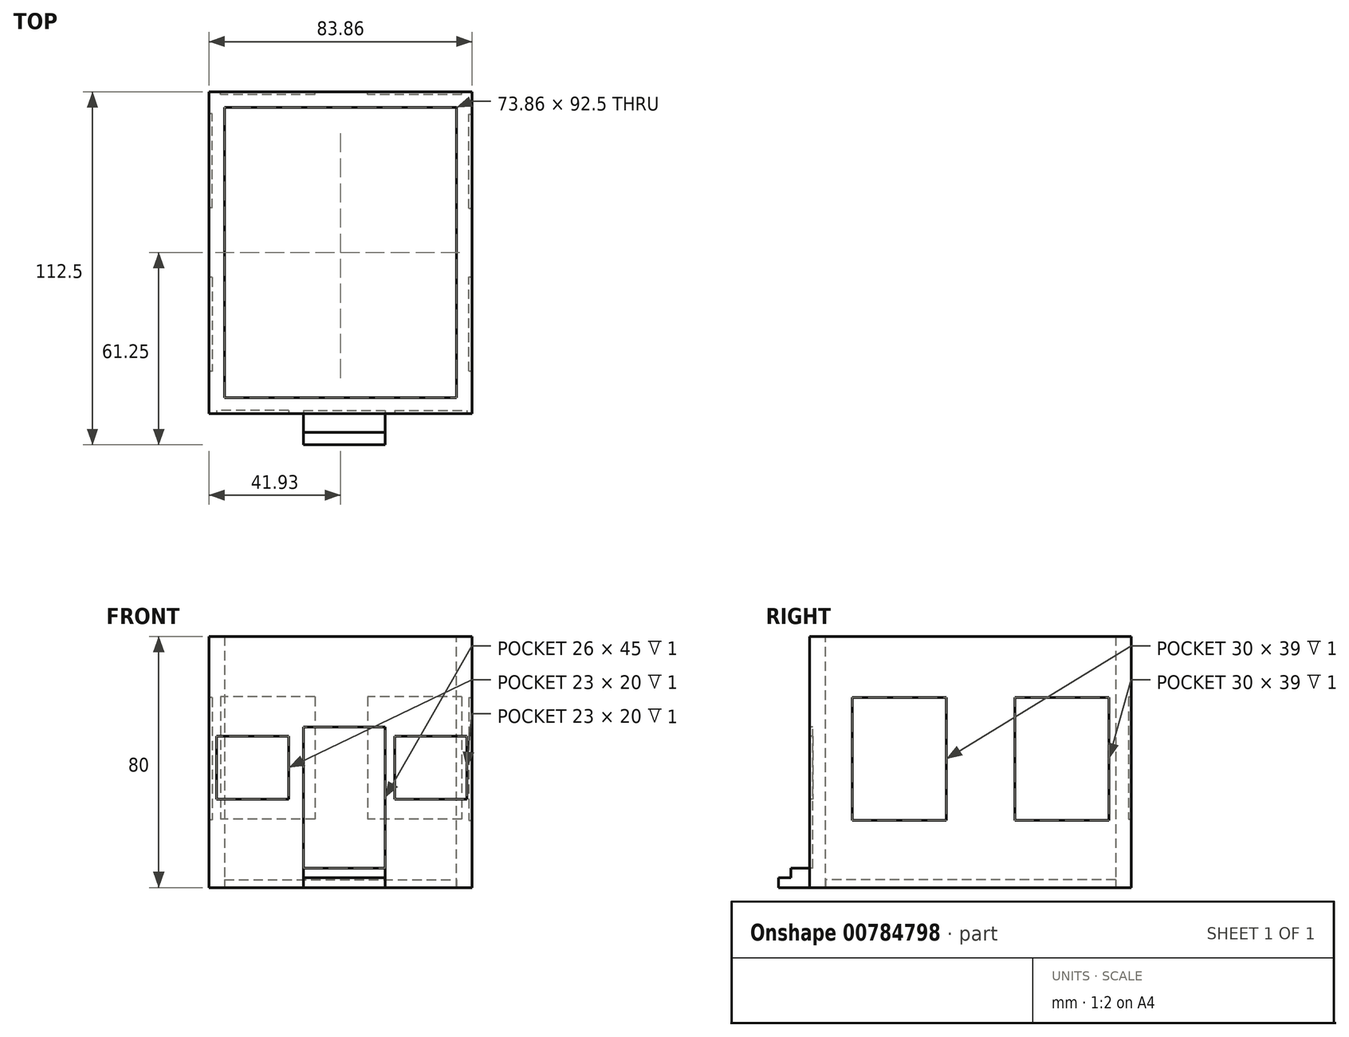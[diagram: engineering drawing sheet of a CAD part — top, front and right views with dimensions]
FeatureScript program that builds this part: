
annotation { "Feature Type Name" : "Feature", "Feature Type Description" : "" }
export const myFeature = defineFeature(function(context is Context, id is Id, definition is map)
    precondition{}
    {
        {
            var Q0;
            Q0=qCreatedBy(makeId("Front.planeOp"),FACE);
            var sketch = newSketch(context, id + "F0", { "sketchPlane" : qUnion([Q0])});
            skLineSegment(sketch, "E0.bottom", {"start": v(-40.68, 40) * mm, "end": v(40.68, 40) * mm});
            skLineSegment(sketch, "E0.top", {"start": v(-40.68, -40) * mm, "end": v(40.68, -40) * mm});
            skLineSegment(sketch, "E0.left", {"start": v(-40.68, 40) * mm, "end": v(-40.68, -40) * mm});
            skLineSegment(sketch, "E0.right", {"start": v(40.68, 40) * mm, "end": v(40.68, -40) * mm});
            skPoint(sketch, "E0.middle", {"position": v(0, 0) * mm});
            skSolve(sketch);
        }
        {
            var Q0;
            Q0 = qSketchRegion(id + "F0", true);
            extrude(context, id + "F1", {"entities" : qUnion([Q0]), "depth" : 2.5 * mm, "offsetDistance" : 25 * mm, "hasSecondDirection" : true, "secondDirectionOppositeDirection" : true, "secondDirectionDepth" : 2.5 * mm});
        }
        {
            var Q0;
            Q0=makeQuery(id+"F1.opExtrude","SWEPT_FACE",FACE,{"disambiguationData":[OSD([sQuery(id+"F0.wireOp",EDGE,"E0.left")])]});
            var sketch = newSketch(context, id + "F2", { "sketchPlane" : qUnion([Q0])});
            skLineSegment(sketch, "E1.bottom", {"start": v(2.5, 40) * mm, "end": v(-97.5, 40) * mm});
            skLineSegment(sketch, "E1.top", {"start": v(2.5, -40) * mm, "end": v(-97.5, -40) * mm});
            skLineSegment(sketch, "E1.left", {"start": v(2.5, 40) * mm, "end": v(2.5, -40) * mm});
            skLineSegment(sketch, "E1.right", {"start": v(-97.5, 40) * mm, "end": v(-97.5, -40) * mm});
            skSolve(sketch);
        }
        {
            var Q0;
            Q0 = qSketchRegion(id + "F2", true);
            extrude(context, id + "F3", {"entities" : qUnion([Q0]), "operationType" : NewBodyOperationType.ADD, "depth" : 2.5 * mm, "offsetDistance" : 25 * mm, "hasSecondDirection" : true, "secondDirectionOppositeDirection" : true, "secondDirectionDepth" : 2.5 * mm});
        }
        {
            var Q0;
            Q0=makeQuery(id+"F3.opExtrude","SWEPT_FACE",FACE,{"disambiguationData":[OSD([sQuery(id+"F2.wireOp",EDGE,"E1.right")])]});
            var sketch = newSketch(context, id + "F4", { "sketchPlane" : qUnion([Q0])});
            skLineSegment(sketch, "E2.bottom", {"start": v(43.18, 40) * mm, "end": v(-38.18, 40) * mm});
            skLineSegment(sketch, "E2.top", {"start": v(43.18, -40) * mm, "end": v(-38.18, -40) * mm});
            skLineSegment(sketch, "E2.left", {"start": v(43.18, 40) * mm, "end": v(43.18, -40) * mm});
            skLineSegment(sketch, "E2.right", {"start": v(-38.18, 40) * mm, "end": v(-38.18, -40) * mm});
            skSolve(sketch);
        }
        {
            var Q0;
            Q0 = qSketchRegion(id + "F4", true);
            extrude(context, id + "F5", {"entities" : qUnion([Q0]), "operationType" : NewBodyOperationType.ADD, "depth" : 2.5 * mm, "offsetDistance" : 25 * mm, "hasSecondDirection" : true, "secondDirectionOppositeDirection" : true, "secondDirectionDepth" : 2.5 * mm});
        }
        {
            var Q0;
            Q0=makeQuery(id+"F5.opExtrude","SWEPT_FACE",FACE,{"disambiguationData":[OSD([sQuery(id+"F4.wireOp",EDGE,"E2.right")])]});
            var sketch = newSketch(context, id + "F6", { "sketchPlane" : qUnion([Q0])});
            skLineSegment(sketch, "E3.bottom", {"start": v(100, 40) * mm, "end": v(0, 40) * mm});
            skLineSegment(sketch, "E3.top", {"start": v(100, -40) * mm, "end": v(0, -40) * mm});
            skLineSegment(sketch, "E3.left", {"start": v(100, 40) * mm, "end": v(100, -40) * mm});
            skLineSegment(sketch, "E3.right", {"start": v(0, 40) * mm, "end": v(0, -40) * mm});
            skSolve(sketch);
        }
        {
            var Q0;
            Q0 = qSketchRegion(id + "F6", true);
            extrude(context, id + "F7", {"entities" : qUnion([Q0]), "operationType" : NewBodyOperationType.ADD, "depth" : 2.5 * mm, "offsetDistance" : 25 * mm, "hasSecondDirection" : true, "secondDirectionOppositeDirection" : true, "secondDirectionDepth" : 2.5 * mm});
        }
        {
            var Q0;
            Q0=makeQuery(id+"F7.boolean.opBoolean","MERGE",FACE,{"derivedFrom":[makeQuery(id+"F5.boolean.opBoolean","MERGE",FACE,{"derivedFrom":[makeQuery(id+"F3.boolean.opBoolean","MERGE",FACE,{"derivedFrom":[makeQuery(id+"F1.opExtrude","SWEPT_FACE",FACE,{"disambiguationData":[OSD([sQuery(id+"F0.wireOp",EDGE,"E0.top")])]}),makeQuery(id+"F3.opExtrude","SWEPT_FACE",FACE,{"disambiguationData":[OSD([sQuery(id+"F2.wireOp",EDGE,"E1.top")])]})]}),makeQuery(id+"F5.opExtrude","SWEPT_FACE",FACE,{"disambiguationData":[OSD([sQuery(id+"F4.wireOp",EDGE,"E2.top")])]})]}),makeQuery(id+"F7.opExtrude","SWEPT_FACE",FACE,{"disambiguationData":[OSD([sQuery(id+"F6.wireOp",EDGE,"E3.top")])]})]});
            var sketch = newSketch(context, id + "F8", { "sketchPlane" : qUnion([Q0])});
            skLineSegment(sketch, "E4.bottom", {"start": v(35.68, -2.5) * mm, "end": v(-38.18, -2.5) * mm});
            skLineSegment(sketch, "E4.top", {"start": v(35.68, -95) * mm, "end": v(-38.18, -95) * mm});
            skLineSegment(sketch, "E4.left", {"start": v(35.68, -2.5) * mm, "end": v(35.68, -95) * mm});
            skLineSegment(sketch, "E4.right", {"start": v(-38.18, -2.5) * mm, "end": v(-38.18, -95) * mm});
            skSolve(sketch);
        }
        {
            var Q0;
            Q0 = qSketchRegion(id + "F8", true);
            extrude(context, id + "F9", {"entities" : qUnion([Q0]), "depth" : 0 * mm, "offsetDistance" : 25 * mm, "hasSecondDirection" : true, "secondDirectionOppositeDirection" : true, "secondDirectionDepth" : 2.5 * mm});
        }
        {
            var Q0;
            Q0=makeQuery(id+"F3.boolean.opBoolean","MERGE",FACE,{"derivedFrom":[makeQuery(id+"F1.opExtrude","CAP_FACE",FACE,{"disambiguationData":[OSD([sQuery(id+"F0.wireOp",EDGE,"E0.bottom"),sQuery(id+"F0.wireOp",EDGE,"E0.top"),sQuery(id+"F0.wireOp",EDGE,"E0.left"),sQuery(id+"F0.wireOp",EDGE,"E0.right")])],"isStart":false}),makeQuery(id+"F3.opExtrude","SWEPT_FACE",FACE,{"disambiguationData":[OSD([sQuery(id+"F2.wireOp",EDGE,"E1.left")])]})]});
            var sketch = newSketch(context, id + "F10", { "sketchPlane" : qUnion([Q0])});
            skLineSegment(sketch, "E5.bottom", {"start": v(-13, -33.85) * mm, "end": v(13, -33.85) * mm});
            skLineSegment(sketch, "E5.top", {"start": v(-13, 11.15) * mm, "end": v(13, 11.15) * mm});
            skLineSegment(sketch, "E5.left", {"start": v(-13, -33.85) * mm, "end": v(-13, 11.15) * mm});
            skLineSegment(sketch, "E5.right", {"start": v(13, -33.85) * mm, "end": v(13, 11.15) * mm});
            skPoint(sketch, "E5.middle", {"position": v(0, -11.35) * mm});
            skSolve(sketch);
        }
        {
            var Q0;
            Q0 = qSketchRegion(id + "F10", true);
            extrude(context, id + "F11", {"entities" : qUnion([Q0]), "operationType" : NewBodyOperationType.REMOVE, "oppositeDirection" : true, "depth" : 1 * mm, "offsetDistance" : 25 * mm, "hasSecondDirection" : true, "secondDirectionOppositeDirection" : false, "secondDirectionDepth" : 0 * mm});
        }
        {
            var Q0;
            Q0=makeQuery(id+"F3.boolean.opBoolean","MERGE",FACE,{"derivedFrom":[makeQuery(id+"F1.opExtrude","CAP_FACE",FACE,{"disambiguationData":[OSD([sQuery(id+"F0.wireOp",EDGE,"E0.bottom"),sQuery(id+"F0.wireOp",EDGE,"E0.top"),sQuery(id+"F0.wireOp",EDGE,"E0.left"),sQuery(id+"F0.wireOp",EDGE,"E0.right")])],"isStart":false}),makeQuery(id+"F3.opExtrude","SWEPT_FACE",FACE,{"disambiguationData":[OSD([sQuery(id+"F2.wireOp",EDGE,"E1.left")])]})]});
            var sketch = newSketch(context, id + "F12", { "sketchPlane" : qUnion([Q0])});
            skLineSegment(sketch, "E6.bottom", {"start": v(-13, -33.85) * mm, "end": v(13, -33.85) * mm});
            skLineSegment(sketch, "E6.top", {"start": v(-13, -40) * mm, "end": v(13, -40) * mm});
            skLineSegment(sketch, "E6.left", {"start": v(-13, -33.85) * mm, "end": v(-13, -40) * mm});
            skLineSegment(sketch, "E6.right", {"start": v(13, -33.85) * mm, "end": v(13, -40) * mm});
            skSolve(sketch);
        }
        {
            var Q0;
            Q0 = qSketchRegion(id + "F12", true);
            extrude(context, id + "F13", {"entities" : qUnion([Q0]), "operationType" : NewBodyOperationType.ADD, "depth" : 6 * mm, "offsetDistance" : 25 * mm});
        }
        {
            var Q0;
            Q0=makeQuery(id+"F3.boolean.opBoolean","MERGE",FACE,{"derivedFrom":[makeQuery(id+"F1.opExtrude","CAP_FACE",FACE,{"disambiguationData":[OSD([sQuery(id+"F0.wireOp",EDGE,"E0.bottom"),sQuery(id+"F0.wireOp",EDGE,"E0.top"),sQuery(id+"F0.wireOp",EDGE,"E0.left"),sQuery(id+"F0.wireOp",EDGE,"E0.right")])],"isStart":false}),makeQuery(id+"F3.opExtrude","SWEPT_FACE",FACE,{"disambiguationData":[OSD([sQuery(id+"F2.wireOp",EDGE,"E1.left")])]})]});
            var sketch = newSketch(context, id + "F14", { "sketchPlane" : qUnion([Q0])});
            skLineSegment(sketch, "E7.bottom", {"start": v(-17.77, 8.2) * mm, "end": v(-40.77, 8.2) * mm});
            skLineSegment(sketch, "E7.top", {"start": v(-17.77, -11.8) * mm, "end": v(-40.77, -11.8) * mm});
            skLineSegment(sketch, "E7.left", {"start": v(-17.77, 8.2) * mm, "end": v(-17.77, -11.8) * mm});
            skLineSegment(sketch, "E7.right", {"start": v(-40.77, 8.2) * mm, "end": v(-40.77, -11.8) * mm});
            skSolve(sketch);
        }
        {
            var Q0;
            Q0 = qSketchRegion(id + "F14", true);
            extrude(context, id + "F15", {"entities" : qUnion([Q0]), "operationType" : NewBodyOperationType.REMOVE, "oppositeDirection" : true, "depth" : 1 * mm, "offsetDistance" : 25 * mm});
        }
        {
            var Q0;
            Q0=makeQuery(id+"F3.boolean.opBoolean","MERGE",FACE,{"derivedFrom":[makeQuery(id+"F1.opExtrude","CAP_FACE",FACE,{"disambiguationData":[OSD([sQuery(id+"F0.wireOp",EDGE,"E0.bottom"),sQuery(id+"F0.wireOp",EDGE,"E0.top"),sQuery(id+"F0.wireOp",EDGE,"E0.left"),sQuery(id+"F0.wireOp",EDGE,"E0.right")])],"isStart":false}),makeQuery(id+"F3.opExtrude","SWEPT_FACE",FACE,{"disambiguationData":[OSD([sQuery(id+"F2.wireOp",EDGE,"E1.left")])]})]});
            var sketch = newSketch(context, id + "F16", { "sketchPlane" : qUnion([Q0])});
            skLineSegment(sketch, "E8.bottom", {"start": v(16.06, 8.2) * mm, "end": v(39.06, 8.2) * mm});
            skLineSegment(sketch, "E8.top", {"start": v(16.06, -11.8) * mm, "end": v(39.06, -11.8) * mm});
            skLineSegment(sketch, "E8.left", {"start": v(16.06, 8.2) * mm, "end": v(16.06, -11.8) * mm});
            skLineSegment(sketch, "E8.right", {"start": v(39.06, 8.2) * mm, "end": v(39.06, -11.8) * mm});
            skSolve(sketch);
        }
        {
            var Q0;
            Q0 = qSketchRegion(id + "F16", true);
            extrude(context, id + "F17", {"entities" : qUnion([Q0]), "operationType" : NewBodyOperationType.REMOVE, "oppositeDirection" : true, "depth" : 1 * mm, "offsetDistance" : 25 * mm});
        }
        {
            var Q0;
            Q0=makeQuery(id+"F3.boolean.opBoolean","MERGE",FACE,{"derivedFrom":[makeQuery(id+"F1.opExtrude","CAP_FACE",FACE,{"disambiguationData":[OSD([sQuery(id+"F0.wireOp",EDGE,"E0.bottom"),sQuery(id+"F0.wireOp",EDGE,"E0.top"),sQuery(id+"F0.wireOp",EDGE,"E0.left"),sQuery(id+"F0.wireOp",EDGE,"E0.right")])],"isStart":false}),makeQuery(id+"F3.opExtrude","SWEPT_FACE",FACE,{"disambiguationData":[OSD([sQuery(id+"F2.wireOp",EDGE,"E1.left")])]})]});
            var sketch = newSketch(context, id + "F18", { "sketchPlane" : qUnion([Q0])});
            skLineSegment(sketch, "E9.bottom", {"start": v(-13, -36.93) * mm, "end": v(13, -36.93) * mm});
            skLineSegment(sketch, "E9.top", {"start": v(-13, -40) * mm, "end": v(13, -40) * mm});
            skLineSegment(sketch, "E9.left", {"start": v(-13, -36.93) * mm, "end": v(-13, -40) * mm});
            skLineSegment(sketch, "E9.right", {"start": v(13, -36.93) * mm, "end": v(13, -40) * mm});
            skSolve(sketch);
        }
        {
            var Q0;
            Q0 = qSketchRegion(id + "F18", true);
            extrude(context, id + "F19", {"entities" : qUnion([Q0]), "operationType" : NewBodyOperationType.ADD, "depth" : 10 * mm, "offsetDistance" : 25 * mm});
        }
        {
            var Q0;
            Q0=makeQuery(id+"F5.boolean.opBoolean","MERGE",FACE,{"derivedFrom":[makeQuery(id+"F3.opExtrude","CAP_FACE",FACE,{"disambiguationData":[OSD([sQuery(id+"F2.wireOp",EDGE,"E1.bottom"),sQuery(id+"F2.wireOp",EDGE,"E1.top"),sQuery(id+"F2.wireOp",EDGE,"E1.left"),sQuery(id+"F2.wireOp",EDGE,"E1.right")])],"isStart":false}),makeQuery(id+"F5.opExtrude","SWEPT_FACE",FACE,{"disambiguationData":[OSD([sQuery(id+"F4.wireOp",EDGE,"E2.left")])]})]});
            var sketch = newSketch(context, id + "F20", { "sketchPlane" : qUnion([Q0])});
            skLineSegment(sketch, "E10.bottom", {"start": v(-40.86, 20.51) * mm, "end": v(-10.86, 20.51) * mm});
            skLineSegment(sketch, "E10.top", {"start": v(-40.86, -18.49) * mm, "end": v(-10.86, -18.49) * mm});
            skLineSegment(sketch, "E10.left", {"start": v(-40.86, 20.51) * mm, "end": v(-40.86, -18.49) * mm});
            skLineSegment(sketch, "E10.right", {"start": v(-10.86, 20.51) * mm, "end": v(-10.86, -18.49) * mm});
            skSolve(sketch);
        }
        {
            var Q0;
            Q0 = qSketchRegion(id + "F20", true);
            extrude(context, id + "F21", {"entities" : qUnion([Q0]), "operationType" : NewBodyOperationType.REMOVE, "oppositeDirection" : true, "depth" : 1 * mm, "offsetDistance" : 25 * mm});
        }
        {
            var Q0;
            Q0=makeQuery(id+"F5.boolean.opBoolean","MERGE",FACE,{"derivedFrom":[makeQuery(id+"F3.opExtrude","CAP_FACE",FACE,{"disambiguationData":[OSD([sQuery(id+"F2.wireOp",EDGE,"E1.bottom"),sQuery(id+"F2.wireOp",EDGE,"E1.top"),sQuery(id+"F2.wireOp",EDGE,"E1.left"),sQuery(id+"F2.wireOp",EDGE,"E1.right")])],"isStart":false}),makeQuery(id+"F5.opExtrude","SWEPT_FACE",FACE,{"disambiguationData":[OSD([sQuery(id+"F4.wireOp",EDGE,"E2.left")])]})]});
            var sketch = newSketch(context, id + "F22", { "sketchPlane" : qUnion([Q0])});
            skLineSegment(sketch, "E11.bottom", {"start": v(-62.94, 20.51) * mm, "end": v(-92.94, 20.51) * mm});
            skLineSegment(sketch, "E11.top", {"start": v(-62.94, -18.49) * mm, "end": v(-92.94, -18.49) * mm});
            skLineSegment(sketch, "E11.left", {"start": v(-62.94, 20.51) * mm, "end": v(-62.94, -18.49) * mm});
            skLineSegment(sketch, "E11.right", {"start": v(-92.94, 20.51) * mm, "end": v(-92.94, -18.49) * mm});
            skSolve(sketch);
        }
        {
            var Q0;
            Q0 = qSketchRegion(id + "F22", true);
            extrude(context, id + "F23", {"entities" : qUnion([Q0]), "operationType" : NewBodyOperationType.REMOVE, "depth" : 0 * mm, "offsetDistance" : 25 * mm, "hasSecondDirection" : true, "secondDirectionOppositeDirection" : true, "secondDirectionDepth" : 1 * mm});
        }
        {
            var Q0;
            Q0=makeQuery(id+"F7.boolean.opBoolean","MERGE",FACE,{"derivedFrom":[makeQuery(id+"F1.opExtrude","SWEPT_FACE",FACE,{"disambiguationData":[OSD([sQuery(id+"F0.wireOp",EDGE,"E0.right")])]}),makeQuery(id+"F7.opExtrude","CAP_FACE",FACE,{"disambiguationData":[OSD([sQuery(id+"F6.wireOp",EDGE,"E3.bottom"),sQuery(id+"F6.wireOp",EDGE,"E3.top"),sQuery(id+"F6.wireOp",EDGE,"E3.left"),sQuery(id+"F6.wireOp",EDGE,"E3.right")])],"isStart":false})]});
            var sketch = newSketch(context, id + "F24", { "sketchPlane" : qUnion([Q0])});
            skLineSegment(sketch, "E12.bottom", {"start": v(11, 20.47) * mm, "end": v(41, 20.47) * mm});
            skLineSegment(sketch, "E12.top", {"start": v(11, -18.53) * mm, "end": v(41, -18.53) * mm});
            skLineSegment(sketch, "E12.left", {"start": v(11, 20.47) * mm, "end": v(11, -18.53) * mm});
            skLineSegment(sketch, "E12.right", {"start": v(41, 20.47) * mm, "end": v(41, -18.53) * mm});
            skSolve(sketch);
        }
        {
            var Q0;
            Q0 = qSketchRegion(id + "F24", true);
            extrude(context, id + "F25", {"entities" : qUnion([Q0]), "operationType" : NewBodyOperationType.REMOVE, "oppositeDirection" : true, "depth" : 1 * mm, "offsetDistance" : 25 * mm});
        }
        {
            var Q0;
            Q0=makeQuery(id+"F7.boolean.opBoolean","MERGE",FACE,{"derivedFrom":[makeQuery(id+"F1.opExtrude","SWEPT_FACE",FACE,{"disambiguationData":[OSD([sQuery(id+"F0.wireOp",EDGE,"E0.right")])]}),makeQuery(id+"F7.opExtrude","CAP_FACE",FACE,{"disambiguationData":[OSD([sQuery(id+"F6.wireOp",EDGE,"E3.bottom"),sQuery(id+"F6.wireOp",EDGE,"E3.top"),sQuery(id+"F6.wireOp",EDGE,"E3.left"),sQuery(id+"F6.wireOp",EDGE,"E3.right")])],"isStart":false})]});
            var sketch = newSketch(context, id + "F26", { "sketchPlane" : qUnion([Q0])});
            skLineSegment(sketch, "E13.bottom", {"start": v(62.81, 20.47) * mm, "end": v(92.81, 20.47) * mm});
            skLineSegment(sketch, "E13.top", {"start": v(62.81, -18.53) * mm, "end": v(92.81, -18.53) * mm});
            skLineSegment(sketch, "E13.left", {"start": v(62.81, 20.47) * mm, "end": v(62.81, -18.53) * mm});
            skLineSegment(sketch, "E13.right", {"start": v(92.81, 20.47) * mm, "end": v(92.81, -18.53) * mm});
            skSolve(sketch);
        }
        {
            var Q0;
            Q0 = qSketchRegion(id + "F26", true);
            extrude(context, id + "F27", {"entities" : qUnion([Q0]), "operationType" : NewBodyOperationType.REMOVE, "oppositeDirection" : true, "depth" : 1 * mm, "offsetDistance" : 25 * mm});
        }
        {
            var Q0;
            Q0=makeQuery(id+"F7.boolean.opBoolean","MERGE",FACE,{"derivedFrom":[makeQuery(id+"F5.opExtrude","CAP_FACE",FACE,{"disambiguationData":[OSD([sQuery(id+"F4.wireOp",EDGE,"E2.bottom"),sQuery(id+"F4.wireOp",EDGE,"E2.top"),sQuery(id+"F4.wireOp",EDGE,"E2.left"),sQuery(id+"F4.wireOp",EDGE,"E2.right")])],"isStart":false}),makeQuery(id+"F7.opExtrude","SWEPT_FACE",FACE,{"disambiguationData":[OSD([sQuery(id+"F6.wireOp",EDGE,"E3.left")])]})]});
            var sketch = newSketch(context, id + "F28", { "sketchPlane" : qUnion([Q0])});
            skLineSegment(sketch, "E14.bottom", {"start": v(-37.39, 20.73) * mm, "end": v(-7.39, 20.73) * mm});
            skLineSegment(sketch, "E14.top", {"start": v(-37.39, -18.27) * mm, "end": v(-7.39, -18.27) * mm});
            skLineSegment(sketch, "E14.left", {"start": v(-37.39, 20.73) * mm, "end": v(-37.39, -18.27) * mm});
            skLineSegment(sketch, "E14.right", {"start": v(-7.39, 20.73) * mm, "end": v(-7.39, -18.27) * mm});
            skSolve(sketch);
        }
        {
            var Q0;
            Q0 = qSketchRegion(id + "F28", true);
            extrude(context, id + "F29", {"entities" : qUnion([Q0]), "operationType" : NewBodyOperationType.REMOVE, "oppositeDirection" : true, "depth" : 1 * mm, "offsetDistance" : 25 * mm});
        }
        {
            var Q0;
            Q0=makeQuery(id+"F7.boolean.opBoolean","MERGE",FACE,{"derivedFrom":[makeQuery(id+"F5.opExtrude","CAP_FACE",FACE,{"disambiguationData":[OSD([sQuery(id+"F4.wireOp",EDGE,"E2.bottom"),sQuery(id+"F4.wireOp",EDGE,"E2.top"),sQuery(id+"F4.wireOp",EDGE,"E2.left"),sQuery(id+"F4.wireOp",EDGE,"E2.right")])],"isStart":false}),makeQuery(id+"F7.opExtrude","SWEPT_FACE",FACE,{"disambiguationData":[OSD([sQuery(id+"F6.wireOp",EDGE,"E3.left")])]})]});
            var sketch = newSketch(context, id + "F30", { "sketchPlane" : qUnion([Q0])});
            skLineSegment(sketch, "E15.bottom", {"start": v(9.41, 20.73) * mm, "end": v(39.41, 20.73) * mm});
            skLineSegment(sketch, "E15.top", {"start": v(9.41, -18.27) * mm, "end": v(39.41, -18.27) * mm});
            skLineSegment(sketch, "E15.left", {"start": v(9.41, 20.73) * mm, "end": v(9.41, -18.27) * mm});
            skLineSegment(sketch, "E15.right", {"start": v(39.41, 20.73) * mm, "end": v(39.41, -18.27) * mm});
            skSolve(sketch);
        }
        {
            var Q0;
            Q0 = qSketchRegion(id + "F30", true);
            extrude(context, id + "F31", {"entities" : qUnion([Q0]), "operationType" : NewBodyOperationType.REMOVE, "oppositeDirection" : true, "depth" : 1 * mm, "offsetDistance" : 25 * mm});
        }
    });
